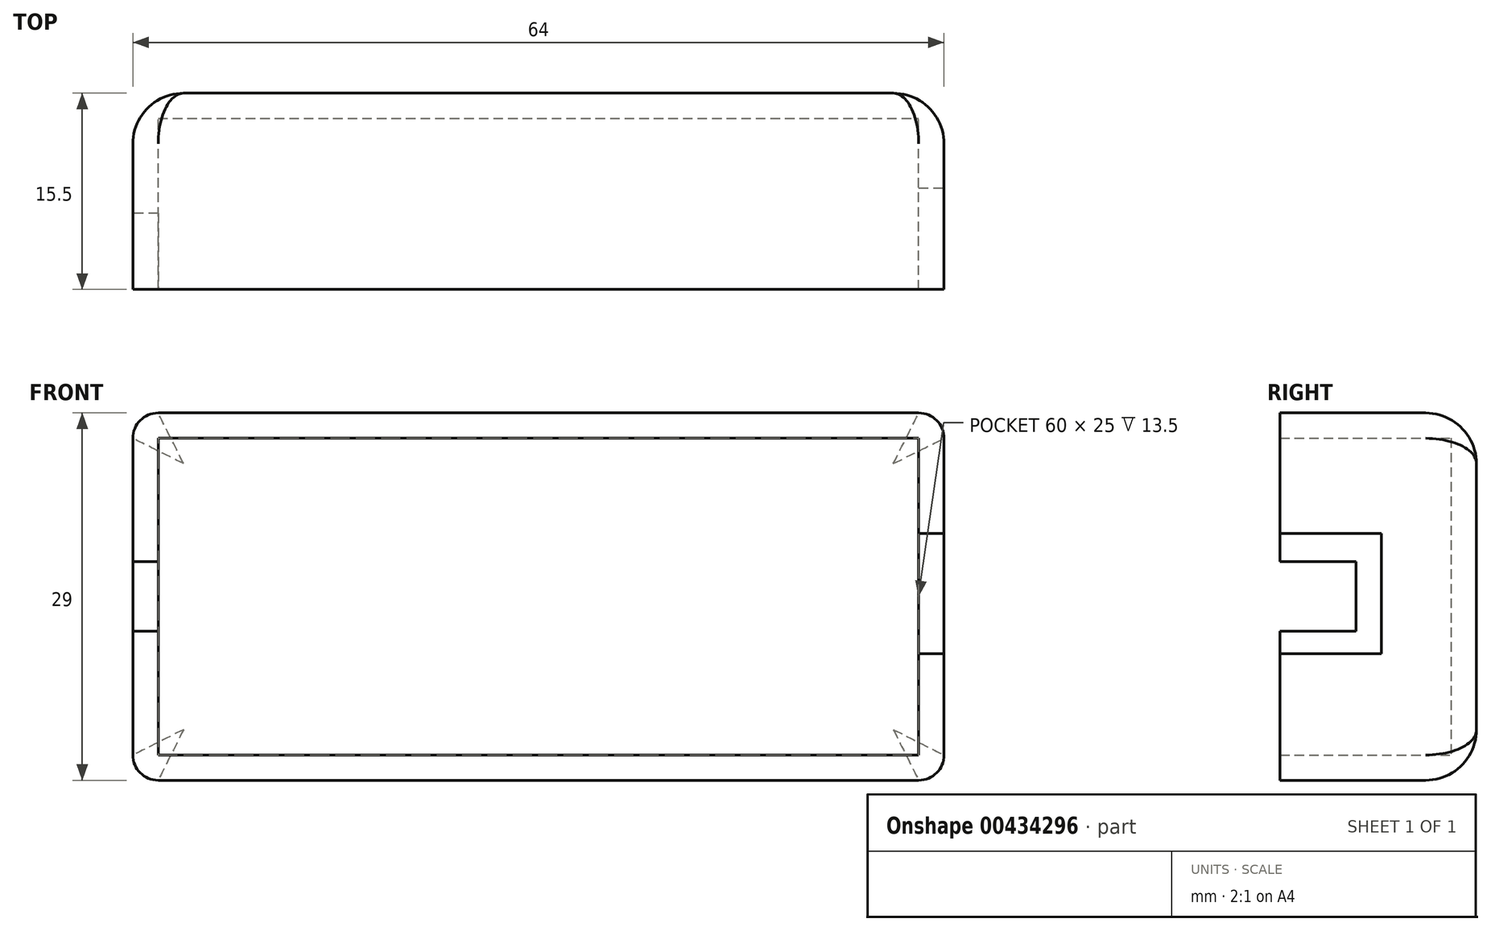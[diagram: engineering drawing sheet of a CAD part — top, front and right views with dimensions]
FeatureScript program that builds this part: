
annotation { "Feature Type Name" : "Feature", "Feature Type Description" : "" }
export const myFeature = defineFeature(function(context is Context, id is Id, definition is map)
    precondition{}
    {
        {
            var Q0;
            Q0=qCreatedBy(makeId("Front.planeOp"),FACE);
            var sketch = newSketch(context, id + "F0", { "sketchPlane" : qUnion([Q0])});
            skLineSegment(sketch, "E0.bottom", {"start": v(-35.13, 4.8) * mm, "end": v(24.87, 4.8) * mm});
            skLineSegment(sketch, "E0.top", {"start": v(-35.13, -20.2) * mm, "end": v(24.87, -20.2) * mm});
            skLineSegment(sketch, "E0.left", {"start": v(-35.13, 4.8) * mm, "end": v(-35.13, -20.2) * mm});
            skLineSegment(sketch, "E0.right", {"start": v(24.87, 4.8) * mm, "end": v(24.87, -20.2) * mm});
            skLineSegment(sketch, "E1.bottom", {"start": v(-37.13, 6.8) * mm, "end": v(26.87, 6.8) * mm});
            skLineSegment(sketch, "E1.top", {"start": v(-37.13, -22.2) * mm, "end": v(26.87, -22.2) * mm});
            skLineSegment(sketch, "E1.left", {"start": v(-37.13, 6.8) * mm, "end": v(-37.13, -22.2) * mm});
            skLineSegment(sketch, "E1.right", {"start": v(26.87, 6.8) * mm, "end": v(26.87, -22.2) * mm});
            skSolve(sketch);
        }
        {
            var Q0;
            Q0=makeQuery(id+"F0.imprint","IMPRINT",FACE,{"disambiguationData":[TD([[makeQuery(id+"F0.imprint","IMPRINT",EDGE,{"derivedFrom":sQuery(id+"F0.wireOp",EDGE,"E0.bottom")}),-1.0]])]});
            extrude(context, id + "F1", {"entities" : qUnion([Q0]), "depth" : 2 * mm});
        }
        {
            var Q0;
            Q0=makeQuery(id+"F0.imprint","IMPRINT",FACE,{"disambiguationData":[TD([[makeQuery(id+"F0.imprint","IMPRINT",EDGE,{"derivedFrom":sQuery(id+"F0.wireOp",EDGE,"E0.bottom")}),1.0]])]});
            extrude(context, id + "F2", {"entities" : qUnion([Q0]), "operationType" : NewBodyOperationType.ADD, "depth" : 15.5 * mm});
        }
        {
            var Q0;
            Q0=makeQuery(id+"F2.opExtrude","SWEPT_FACE",FACE,{"disambiguationData":[OSD([sQuery(id+"F0.wireOp",EDGE,"E1.right")])]});
            var sketch = newSketch(context, id + "F3", { "sketchPlane" : qUnion([Q0])});
            skLineSegment(sketch, "E2.bottom", {"start": v(-15.5, -2.7) * mm, "end": v(-7.5, -2.7) * mm});
            skLineSegment(sketch, "E2.top", {"start": v(-15.5, -12.2) * mm, "end": v(-7.5, -12.2) * mm});
            skLineSegment(sketch, "E2.left", {"start": v(-15.5, -2.7) * mm, "end": v(-15.5, -12.2) * mm});
            skLineSegment(sketch, "E2.right", {"start": v(-7.5, -2.7) * mm, "end": v(-7.5, -12.2) * mm});
            skSolve(sketch);
        }
        {
            var Q0;
            Q0=makeQuery(id+"F3.imprint","IMPRINT",FACE,{"disambiguationData":[TD([[makeQuery(id+"F3.imprint","IMPRINT",EDGE,{"derivedFrom":sQuery(id+"F3.wireOp",EDGE,"E2.bottom")}),-1.0]])]});
            extrude(context, id + "F4", {"entities" : qUnion([Q0]), "operationType" : NewBodyOperationType.REMOVE, "oppositeDirection" : true, "depth" : 25 * mm});
        }
        {
            var Q0;
            Q0=makeQuery(id+"F2.opExtrude","SWEPT_FACE",FACE,{"disambiguationData":[OSD([sQuery(id+"F0.wireOp",EDGE,"E1.left")])]});
            var sketch = newSketch(context, id + "F5", { "sketchPlane" : qUnion([Q0])});
            skLineSegment(sketch, "E3.bottom", {"start": v(15.5, -4.92) * mm, "end": v(9.5, -4.92) * mm});
            skLineSegment(sketch, "E3.top", {"start": v(15.5, -10.42) * mm, "end": v(9.5, -10.42) * mm});
            skLineSegment(sketch, "E3.left", {"start": v(15.5, -4.92) * mm, "end": v(15.5, -10.42) * mm});
            skLineSegment(sketch, "E3.right", {"start": v(9.5, -4.92) * mm, "end": v(9.5, -10.42) * mm});
            skSolve(sketch);
        }
        {
            var Q0;
            Q0=makeQuery(id+"F5.imprint","IMPRINT",FACE,{"disambiguationData":[TD([[makeQuery(id+"F5.imprint","IMPRINT",EDGE,{"derivedFrom":sQuery(id+"F5.wireOp",EDGE,"E3.bottom")}),1.0]])]});
            extrude(context, id + "F6", {"entities" : qUnion([Q0]), "operationType" : NewBodyOperationType.REMOVE, "oppositeDirection" : true, "depth" : 25 * mm});
        }
        {
            var Q0;
            {var subQ0=sQuery(id+"F0.wireOp",EDGE,"E0.right");var subQ1=sQuery(id+"F0.wireOp",EDGE,"E0.left");var subQ2=sQuery(id+"F0.wireOp",EDGE,"E0.top");var subQ3=sQuery(id+"F0.wireOp",EDGE,"E0.bottom");Q0=makeQuery(id+"F2.boolean.opBoolean","MERGE",FACE,{"derivedFrom":[makeQuery(id+"F1.opExtrude","CAP_FACE",FACE,{"disambiguationData":[OSD([subQ3,subQ2,subQ1,subQ0])],"isStart":true}),makeQuery(id+"F2.opExtrude","CAP_FACE",FACE,{"disambiguationData":[OSD([subQ3,subQ2,subQ1,subQ0,sQuery(id+"F0.wireOp",EDGE,"E1.bottom"),sQuery(id+"F0.wireOp",EDGE,"E1.top"),sQuery(id+"F0.wireOp",EDGE,"E1.left"),sQuery(id+"F0.wireOp",EDGE,"E1.right")])],"isStart":true})]});}
            fillet(context, id + "F7", {"entities" : qUnion([Q0]), "radius" : 4 * mm, "tangentPropagation" : true, "allowEdgeOverflow" : false});
        }
        {
            var Q0;
            Q0=makeQuery(id+"F2.opExtrude","SWEPT_EDGE",EDGE,{"disambiguationData":[OSD([sQuery(id+"F0.wireOp",EDGE,"E1.top"),sQuery(id+"F0.wireOp",EDGE,"E1.left")])]});
            var Q1;
            Q1=makeQuery(id+"F2.opExtrude","SWEPT_EDGE",EDGE,{"disambiguationData":[OSD([sQuery(id+"F0.wireOp",EDGE,"E1.top"),sQuery(id+"F0.wireOp",EDGE,"E1.right")])]});
            var Q2;
            Q2=makeQuery(id+"F2.opExtrude","SWEPT_EDGE",EDGE,{"disambiguationData":[OSD([sQuery(id+"F0.wireOp",EDGE,"E1.bottom"),sQuery(id+"F0.wireOp",EDGE,"E1.right")])]});
            var Q3;
            Q3=makeQuery(id+"F2.opExtrude","SWEPT_EDGE",EDGE,{"disambiguationData":[OSD([sQuery(id+"F0.wireOp",EDGE,"E1.bottom"),sQuery(id+"F0.wireOp",EDGE,"E1.left")])]});
            fillet(context, id + "F8", {"entities" : qUnion([Q0, Q1, Q2, Q3]), "radius" : 2 * mm, "tangentPropagation" : true, "allowEdgeOverflow" : false});
        }
    });
